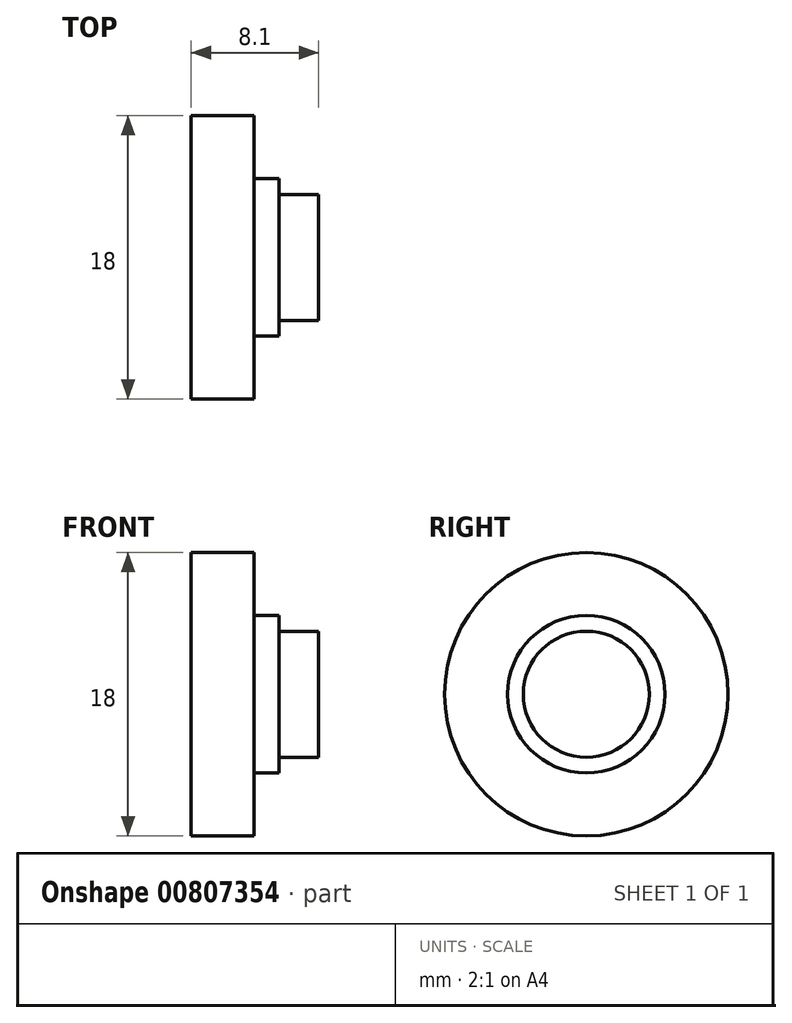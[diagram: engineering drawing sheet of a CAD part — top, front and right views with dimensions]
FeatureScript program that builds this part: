
annotation { "Feature Type Name" : "Feature", "Feature Type Description" : "" }
export const myFeature = defineFeature(function(context is Context, id is Id, definition is map)
    precondition{}
    {
        {
            var Q0;
            Q0=qCreatedBy(makeId("Front.planeOp"),FACE);
            var sketch = newSketch(context, id + "F0", { "sketchPlane" : qUnion([Q0])});
            skLineSegment(sketch, "E0.bottom", {"start": v(-7.15, 0) * mm, "end": v(-5.55, 0) * mm});
            skLineSegment(sketch, "E0.top", {"start": v(-7.15, 5) * mm, "end": v(-5.55, 5) * mm});
            skLineSegment(sketch, "E0.left", {"start": v(-7.15, 0) * mm, "end": v(-7.15, 5) * mm});
            skLineSegment(sketch, "E0.right", {"start": v(-5.55, 0) * mm, "end": v(-5.55, 5) * mm});
            skLineSegment(sketch, "E1.bottom", {"start": v(-5.55, 4) * mm, "end": v(-3.05, 4) * mm});
            skLineSegment(sketch, "E1.top", {"start": v(-5.55, 0) * mm, "end": v(-3.05, 0) * mm});
            skLineSegment(sketch, "E1.left", {"start": v(-5.55, 4) * mm, "end": v(-5.55, 0) * mm});
            skLineSegment(sketch, "E1.right", {"start": v(-3.05, 4) * mm, "end": v(-3.05, 0) * mm});
            skLineSegment(sketch, "E2", {"start": v(-13.2, 0) * mm, "end": v(7.6, 0) * mm, "construction": true});
            skLineSegment(sketch, "E3.bottom", {"start": v(-7.15, 0) * mm, "end": v(-11.15, 0) * mm});
            skLineSegment(sketch, "E3.top", {"start": v(-7.15, 9) * mm, "end": v(-11.15, 9) * mm});
            skLineSegment(sketch, "E3.left", {"start": v(-7.15, 0) * mm, "end": v(-7.15, 9) * mm});
            skLineSegment(sketch, "E3.right", {"start": v(-11.15, 8.2) * mm, "end": v(-11.15, 9) * mm});
            skPoint(sketch, "E4.center.orphan", {"position": v(-27.1, 0) * mm});
            skPoint(sketch, "E4.end.orphan", {"position": v(-9.17, 0) * mm});
            skLineSegment(sketch, "E5", {"start": v(-11.15, 0) * mm, "end": v(-11.15, 8.2) * mm});
            skSolve(sketch);
        }
        {
            var Q0;
            Q0 = qSketchRegion(id + "F0", true);
            var Q1;
            Q1=sQuery(id+"F0.wireOp",EDGE,"E2");
            revolve(context, id + "F1", {"surfaceOperationType" : NewSurfaceOperationType.NEW, "entities" : qUnion([Q0]), "axis" : qUnion([Q1]), "revolveType" : RevolveType.FULL});
        }
    });
